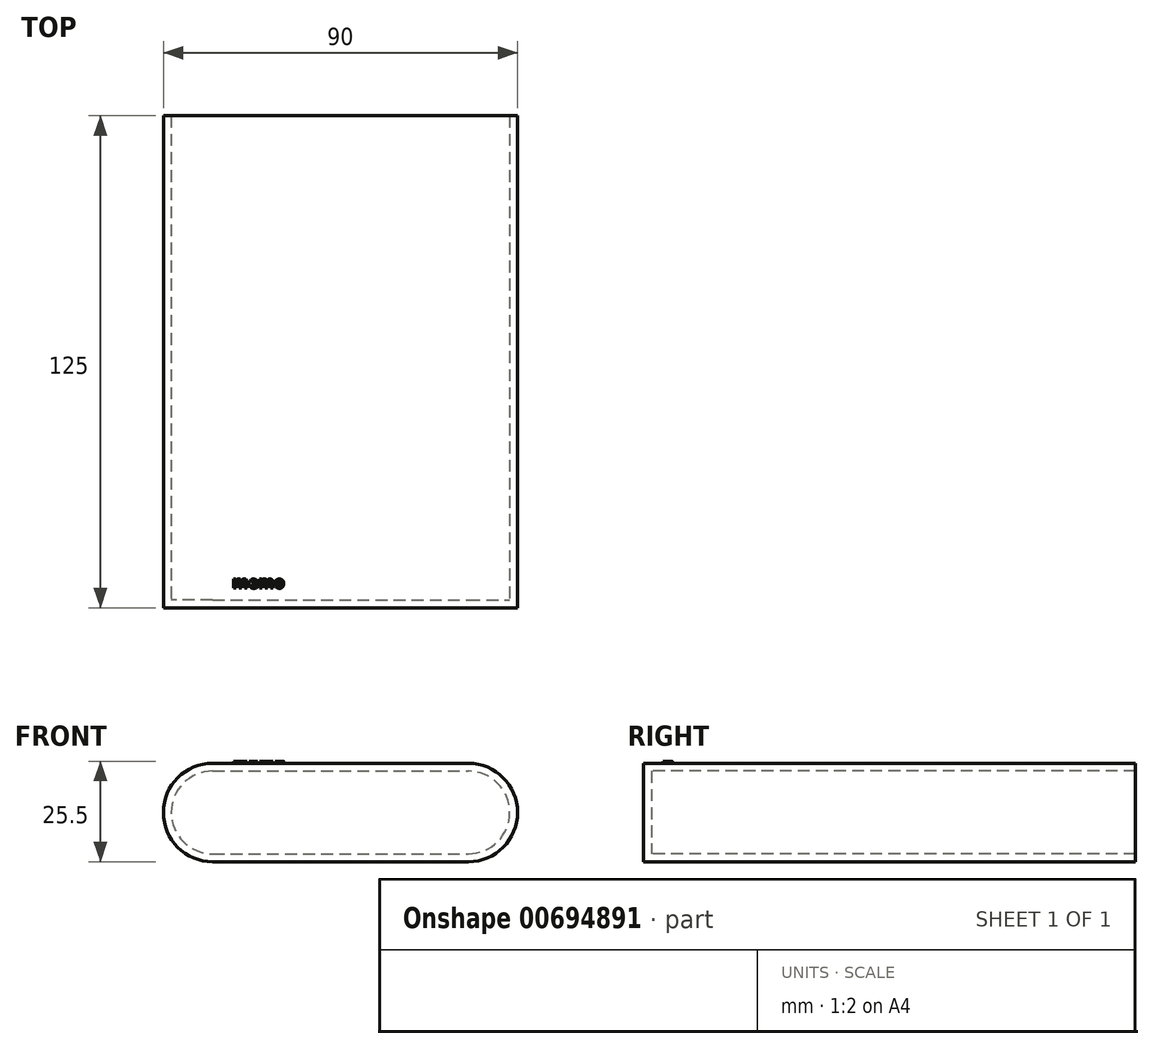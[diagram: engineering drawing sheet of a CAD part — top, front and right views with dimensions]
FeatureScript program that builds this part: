
annotation { "Feature Type Name" : "Feature", "Feature Type Description" : "" }
export const myFeature = defineFeature(function(context is Context, id is Id, definition is map)
    precondition{}
    {
        {
            var Q0;
            Q0=qCreatedBy(makeId("Front.planeOp"),FACE);
            var sketch = newSketch(context, id + "F0", { "sketchPlane" : qUnion([Q0])});
            skPoint(sketch, "E0.middle", {"position": v(0, -12.5) * mm});
            skLineSegment(sketch, "E1.bottom", {"start": v(-32.5, 0) * mm, "end": v(32.5, 0) * mm});
            skLineSegment(sketch, "E1.top", {"start": v(-32.5, -25) * mm, "end": v(32.5, -25) * mm});
            skLineSegment(sketch, "E2.bottom", {"start": v(-32.5, -2) * mm, "end": v(32.5, -2) * mm});
            skLineSegment(sketch, "E2.top", {"start": v(-32.5, -23) * mm, "end": v(32.5, -23) * mm});
            skArc(sketch, "E3", {"start": v(32.5, -25) * mm, "mid": v(45, -12.5) * mm, "end": v(32.5, 0) * mm});
            skArc(sketch, "E4", {"start": v(-32.5, -2) * mm, "mid": v(-43, -12.5) * mm, "end": v(-32.5, -23) * mm});
            skArc(sketch, "E5", {"start": v(-32.5, 0) * mm, "mid": v(-45, -12.5) * mm, "end": v(-32.5, -25) * mm});
            skArc(sketch, "E6", {"start": v(32.5, -23) * mm, "mid": v(43, -12.5) * mm, "end": v(32.5, -2) * mm});
            skSolve(sketch);
        }
        {
            var Q0;
            Q0 = qSketchRegion(id + "F0", true);
            extrude(context, id + "F1", {"entities" : qUnion([Q0]), "depth" : -125 * mm, "offsetDistance" : 25 * mm});
        }
        {
            var Q0;
            Q0=makeQuery(id+"F0.imprint","IMPRINT",FACE,{"disambiguationData":[TD([[makeQuery(id+"F0.imprint","IMPRINT",EDGE,{"derivedFrom":sQuery(id+"F0.wireOp",EDGE,"E2.bottom")}),-1.0]])]});
            extrude(context, id + "F2", {"entities" : qUnion([Q0]), "operationType" : NewBodyOperationType.ADD, "depth" : -2 * mm, "offsetDistance" : 25 * mm});
        }
        {
            var Q0;
            Q0=qCreatedBy(makeId("Top.planeOp"),FACE);
            var sketch = newSketch(context, id + "F3", { "sketchPlane" : qUnion([Q0])});
            skLineSegment(sketch, "E7", {"start": v(-19.49, 0) * mm, "end": v(-19.49, 5) * mm});
            skLineSegment(sketch, "E8", {"start": v(-19.49, 5) * mm, "end": v(-32.47, 5) * mm, "construction": true});
            skLineSegment(sketch, "E9", {"start": v(-32.47, 5) * mm, "end": v(-27.47, 5) * mm, "construction": true});
            skText(sketch, "E10", { "text": "memo", "fontName": "OpenSans-Bold.ttf"});
            const initialGuessF3  = {"E10": [-0.02747, 0.005, 1, 0, 0.003]};
            skSetInitialGuess(sketch, initialGuessF3);
            skSolve(sketch);
        }
        {
            var Q0;
            Q0 = qSketchRegion(id + "F3", true);
            extrude(context, id + "F4", {"entities" : qUnion([Q0]), "operationType" : NewBodyOperationType.ADD, "depth" : 0.5 * mm, "offsetDistance" : 25 * mm});
        }
    });
